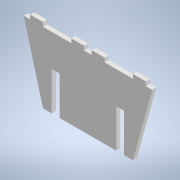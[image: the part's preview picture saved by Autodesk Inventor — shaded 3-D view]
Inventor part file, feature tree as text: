
AUTODESK INVENTOR PART (.ipt)
format: ipt  version: 2022 (Build 260153000, 153)  size: 136,192 bytes
history: native  units: mm
features: reference x5, other x4, extrude x1, sketch x1
ambient origin geometry x8: Origin, YZ Plane, XZ Plane, XY Plane, X Axis, Y Axis, Z Axis, Center Point
bodies: Solid1 (feature_tree)
feature tree (11):
  extrude  "Extrusion1"  Depth=35.0mm
  sketch  "Sketch1"  dims[d0=55.0mm d1=35.0mm d2=50.0mm d3=25.0mm d4=30.0mm d5=6.2mm d6=3.2mm d7=10.0mm d8=3.0mm d9=3.2mm d10=0.0mm d11=3.2mm d12=10.0mm d13=5.0mm]
  reference  "Reference1"
  reference  "Reference2"
  reference  "Reference3"
  reference  "Reference4"
  reference  "Reference5"
  other  "<userpath>\OneDrive\Escritorio\Mini_Proyecto_Diseno\Diseno_18012\Modelo_MPD\Carril.iam"
  other  "Carril.iam"
  other  "Base:1"
  other  "Base:2"
